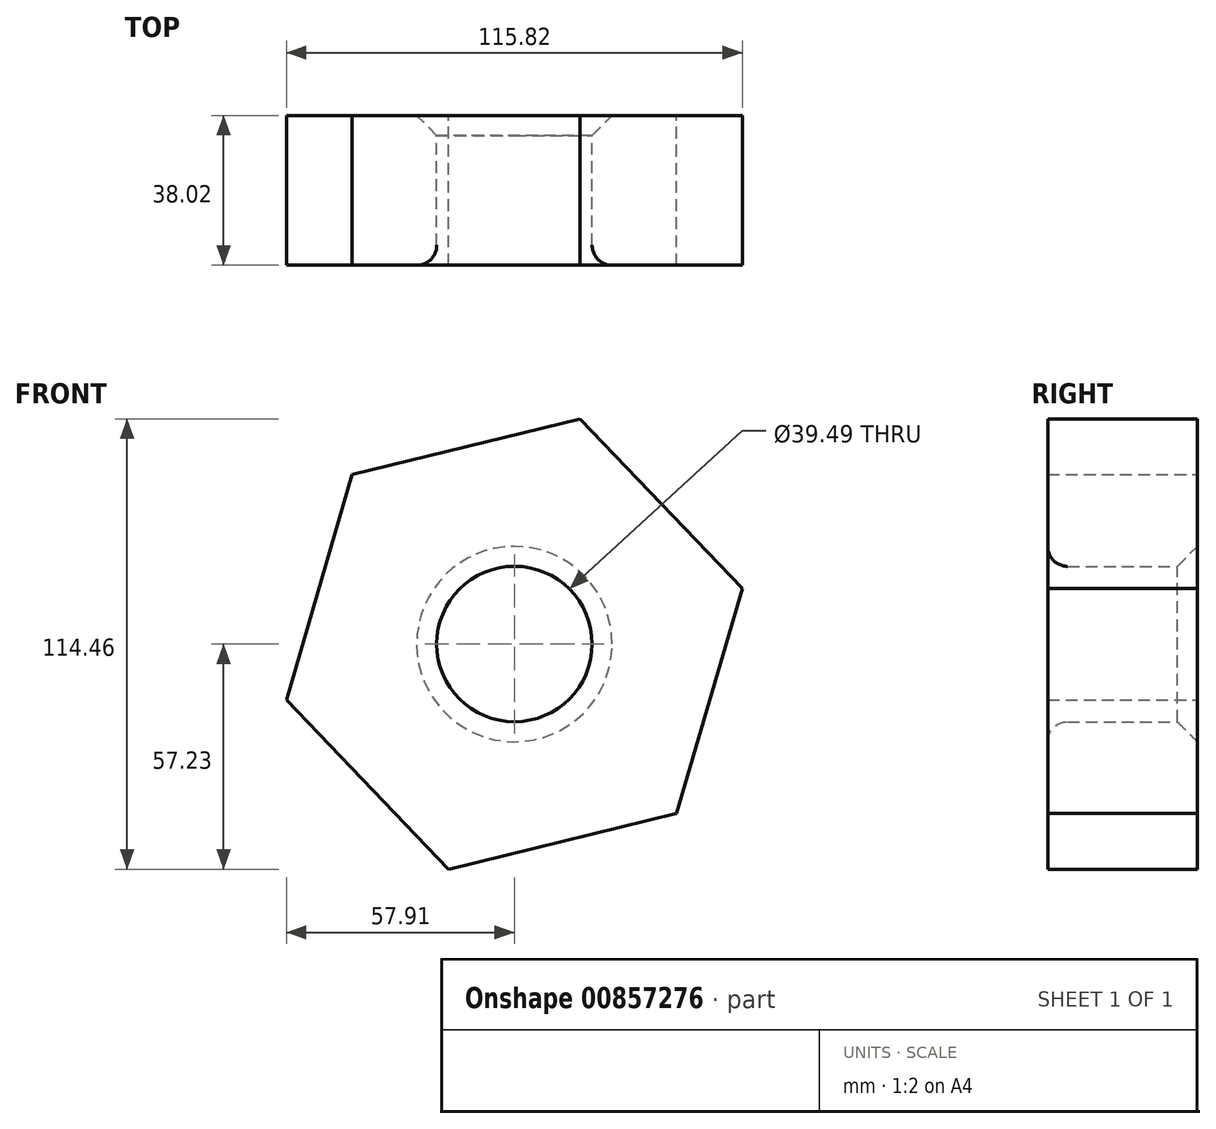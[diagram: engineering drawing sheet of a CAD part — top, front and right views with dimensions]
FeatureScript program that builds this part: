
annotation { "Feature Type Name" : "Feature", "Feature Type Description" : "" }
export const myFeature = defineFeature(function(context is Context, id is Id, definition is map)
    precondition{}
    {
        {
            var Q0;
            Q0=qCreatedBy(makeId("Front.planeOp"),FACE);
            var sketch = newSketch(context, id + "F0", { "sketchPlane" : qUnion([Q0])});
            skLineSegment(sketch, "E0", {"start": v(0, 62.51) * mm, "end": v(0, -82.55) * mm, "construction": true});
            skLineSegment(sketch, "E1", {"start": v(-68.13, 0) * mm, "end": v(74.81, 0) * mm, "construction": true});
            skCircle(sketch, "E2.cCircle", {"center": v(0, 0) * mm, "radius": 51.63 * mm, "construction": true});
            skLineSegment(sketch, "E2.0", {"start": v(57.9, 14.16) * mm, "end": v(41.22, -43.07) * mm});
            skLineSegment(sketch, "E2.1", {"start": v(41.22, -43.07) * mm, "end": v(-16.69, -57.23) * mm});
            skLineSegment(sketch, "E2.2", {"start": v(-16.69, -57.23) * mm, "end": v(-57.9, -14.16) * mm});
            skLineSegment(sketch, "E2.3", {"start": v(-57.9, -14.16) * mm, "end": v(-41.22, 43.07) * mm});
            skLineSegment(sketch, "E2.4", {"start": v(-41.22, 43.07) * mm, "end": v(16.69, 57.23) * mm});
            skLineSegment(sketch, "E2.5", {"start": v(16.69, 57.23) * mm, "end": v(57.9, 14.16) * mm});
            skPoint(sketch, "E2.0.midPoint", {"position": v(49.56, -14.45) * mm});
            skCircle(sketch, "E3", {"center": v(0, 0) * mm, "radius": 19.74 * mm});
            skSolve(sketch);
        }
        {
            var Q0;
            Q0 = qSketchRegion(id + "F0", true);
            extrude(context, id + "F1", {"entities" : qUnion([Q0]), "endBound" : BoundingType.SYMMETRIC, "depth" : 38 * mm, "offsetDistance" : 25.4 * mm});
        }
        {
            var Q0;
            Q0=makeQuery(id+"F1.opExtrude","CAP_EDGE",EDGE,{"disambiguationData":[OSD([sQuery(id+"F0.wireOp",EDGE,"E3")])],"isStart":false});
            fillet(context, id + "F2", {"entities" : qUnion([Q0]), "radius" : 5.08 * mm, "allowEdgeOverflow" : false});
        }
        {
            var Q0;
            Q0=makeQuery(id+"F1.opExtrude","CAP_EDGE",EDGE,{"disambiguationData":[OSD([sQuery(id+"F0.wireOp",EDGE,"E3")])],"isStart":true});
            chamfer(context, id + "F3", {"entities" : qUnion([Q0]), "width" : 5.08 * mm, "tangentPropagation" : true});
        }
    });
